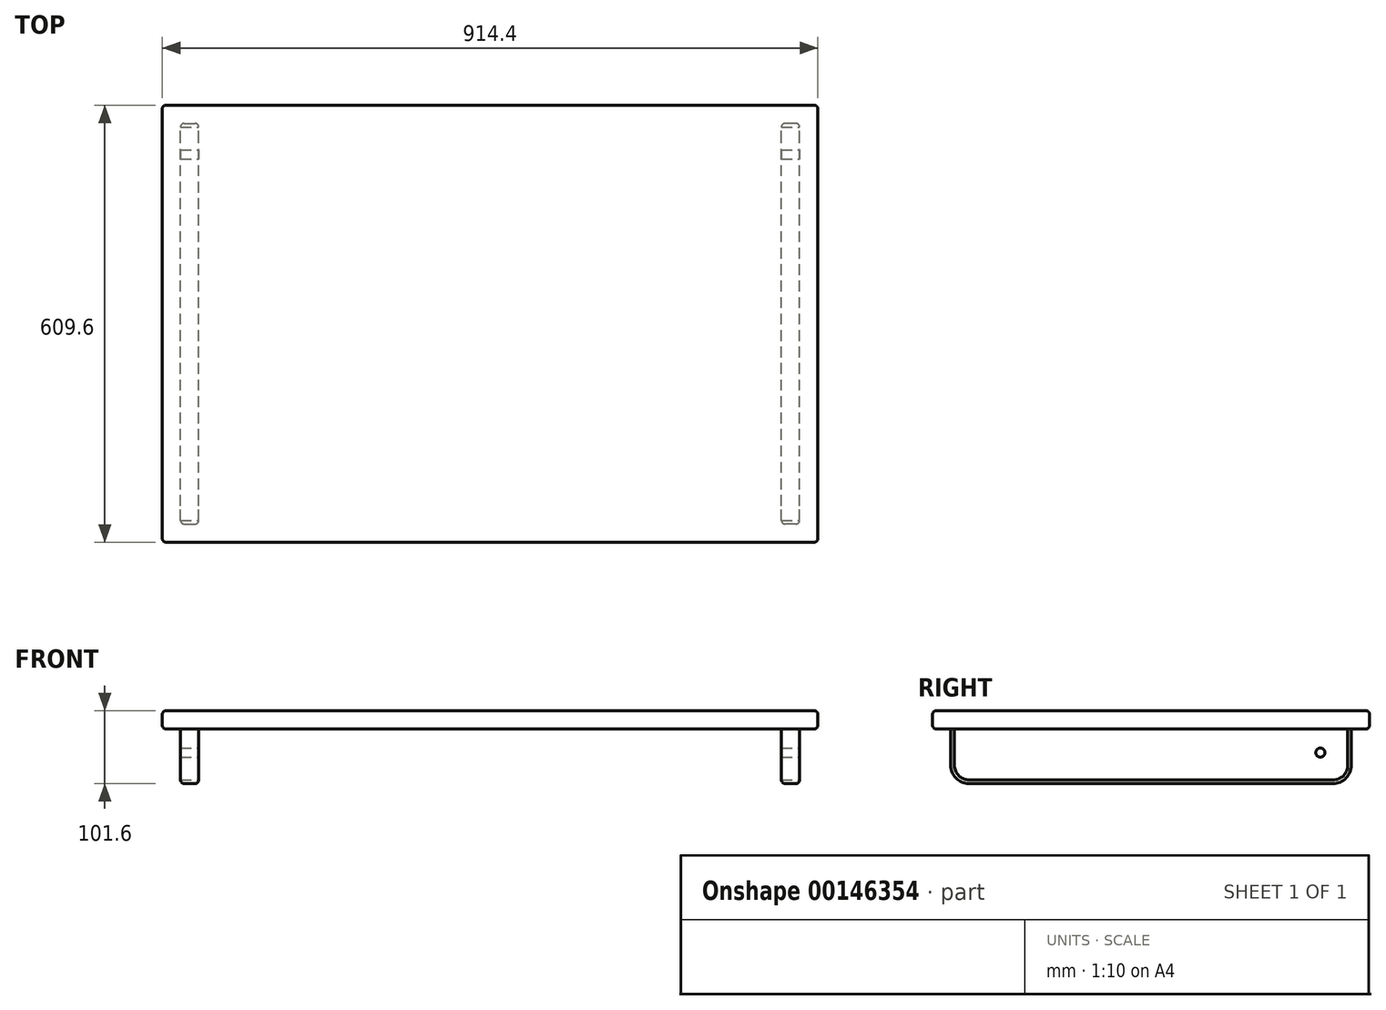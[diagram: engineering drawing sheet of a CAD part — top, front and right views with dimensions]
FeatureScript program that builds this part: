
annotation { "Feature Type Name" : "Feature", "Feature Type Description" : "" }
export const myFeature = defineFeature(function(context is Context, id is Id, definition is map)
    precondition{}
    {
        {
            var Q0;
            Q0=qCreatedBy(makeId("Top.planeOp"),FACE);
            var sketch = newSketch(context, id + "F0", { "sketchPlane" : qUnion([Q0])});
            skLineSegment(sketch, "E0.bottom", {"start": v(-431.8, 279.4) * mm, "end": v(431.8, 279.4) * mm, "construction": true});
            skLineSegment(sketch, "E0.top", {"start": v(-431.8, -279.4) * mm, "end": v(0, -279.4) * mm, "construction": true});
            skLineSegment(sketch, "E0.left", {"start": v(-431.8, 279.4) * mm, "end": v(-431.8, -279.4) * mm, "construction": true});
            skLineSegment(sketch, "E0.right", {"start": v(431.8, 279.4) * mm, "end": v(431.8, 0) * mm, "construction": true});
            skPoint(sketch, "E0.middle", {"position": v(0, 0) * mm});
            skLineSegment(sketch, "E1", {"start": v(0, -279.4) * mm, "end": v(215.9, -279.4) * mm, "construction": true});
            skLineSegment(sketch, "E2", {"start": v(215.9, -279.4) * mm, "end": v(323.85, -279.4) * mm, "construction": true});
            skLineSegment(sketch, "E3", {"start": v(323.85, -279.4) * mm, "end": v(377.82, -279.4) * mm, "construction": true});
            skLineSegment(sketch, "E4", {"start": v(377.82, -279.4) * mm, "end": v(404.81, -279.4) * mm, "construction": true});
            skLineSegment(sketch, "E5", {"start": v(404.81, -279.4) * mm, "end": v(418.3, -279.4) * mm, "construction": true});
            skLineSegment(sketch, "E6", {"start": v(431.8, 0) * mm, "end": v(431.8, -139.7) * mm, "construction": true});
            skLineSegment(sketch, "E7", {"start": v(431.8, -139.7) * mm, "end": v(431.8, -209.55) * mm, "construction": true});
            skLineSegment(sketch, "E8", {"start": v(431.8, -209.55) * mm, "end": v(431.8, -244.48) * mm, "construction": true});
            skLineSegment(sketch, "E9", {"start": v(431.8, -244.48) * mm, "end": v(431.8, -261.94) * mm, "construction": true});
            skLineSegment(sketch, "E10", {"start": v(431.8, -261.94) * mm, "end": v(431.8, -270.67) * mm, "construction": true});
            skLineSegment(sketch, "E11", {"start": v(418.3, -279.4) * mm, "end": v(425.05, -279.4) * mm, "construction": true});
            skLineSegment(sketch, "E12", {"start": v(431.8, -270.67) * mm, "end": v(431.8, -275.03) * mm, "construction": true});
            skLineSegment(sketch, "E13", {"start": v(425.05, -279.4) * mm, "end": v(431.8, -279.4) * mm, "construction": true});
            skLineSegment(sketch, "E14", {"start": v(431.8, -275.03) * mm, "end": v(431.8, -279.4) * mm, "construction": true});
            skLineSegment(sketch, "E15", {"start": v(0, 279.4) * mm, "end": v(0, -279.4) * mm, "construction": true});
            skLineSegment(sketch, "E16", {"start": v(0, 0) * mm, "end": v(431.8, 0) * mm, "construction": true});
            skLineSegment(sketch, "E17", {"start": v(215.9, 0) * mm, "end": v(215.9, -279.4) * mm, "construction": true});
            skLineSegment(sketch, "E18", {"start": v(215.9, -139.7) * mm, "end": v(431.8, -139.7) * mm, "construction": true});
            skLineSegment(sketch, "E19", {"start": v(323.85, -139.7) * mm, "end": v(323.85, -279.4) * mm, "construction": true});
            skLineSegment(sketch, "E20", {"start": v(323.85, -209.55) * mm, "end": v(431.8, -209.55) * mm, "construction": true});
            skLineSegment(sketch, "E21", {"start": v(377.82, -209.55) * mm, "end": v(377.82, -279.4) * mm, "construction": true});
            skLineSegment(sketch, "E22", {"start": v(377.82, -244.48) * mm, "end": v(431.8, -244.48) * mm, "construction": true});
            skLineSegment(sketch, "E23", {"start": v(404.81, -244.48) * mm, "end": v(404.81, -279.4) * mm, "construction": true});
            skLineSegment(sketch, "E24", {"start": v(404.81, -261.94) * mm, "end": v(431.8, -261.94) * mm, "construction": true});
            skLineSegment(sketch, "E25", {"start": v(418.3, -261.94) * mm, "end": v(418.3, -279.4) * mm, "construction": true});
            skLineSegment(sketch, "E26", {"start": v(418.3, -270.67) * mm, "end": v(431.8, -270.67) * mm, "construction": true});
            skLineSegment(sketch, "E27", {"start": v(425.05, -270.67) * mm, "end": v(425.05, -279.4) * mm, "construction": true});
            skLineSegment(sketch, "E28", {"start": v(425.05, -275.03) * mm, "end": v(431.8, -275.03) * mm, "construction": true});
            skSolve(sketch);
        }
        {
            var Q0;
            Q0=qCreatedBy(makeId("Top.planeOp"),FACE);
            var sketch = newSketch(context, id + "F1", { "sketchPlane" : qUnion([Q0])});
            skLineSegment(sketch, "E29.bottom", {"start": v(457.2, 304.8) * mm, "end": v(-457.2, 304.8) * mm});
            skLineSegment(sketch, "E29.top", {"start": v(457.2, -304.8) * mm, "end": v(-457.2, -304.8) * mm});
            skLineSegment(sketch, "E29.left", {"start": v(457.2, 304.8) * mm, "end": v(457.2, -304.8) * mm});
            skLineSegment(sketch, "E29.right", {"start": v(-457.2, 304.8) * mm, "end": v(-457.2, -304.8) * mm});
            skPoint(sketch, "E29.middle", {"position": v(0, 0) * mm});
            skSolve(sketch);
        }
        {
            var Q0;
            Q0=makeQuery(id+"F1.imprint","IMPRINT",FACE,{"disambiguationData":[TD([[makeQuery(id+"F1.imprint","IMPRINT",EDGE,{"derivedFrom":sQuery(id+"F1.wireOp",EDGE,"E29.bottom")}),1.0]])]});
            extrude(context, id + "F2", {"entities" : qUnion([Q0]), "depth" : 25.4 * mm});
        }
        {
            var Q0;
            Q0=makeQuery(id+"F2.opExtrude","SWEPT_EDGE",EDGE,{"disambiguationData":[OSD([sQuery(id+"F1.wireOp",EDGE,"E29.bottom"),sQuery(id+"F1.wireOp",EDGE,"E29.right")])]});
            var Q1;
            Q1=makeQuery(id+"F2.opExtrude","CAP_EDGE",EDGE,{"disambiguationData":[OSD([sQuery(id+"F1.wireOp",EDGE,"E29.right")])],"isStart":false});
            var Q2;
            Q2=makeQuery(id+"F2.opExtrude","SWEPT_EDGE",EDGE,{"disambiguationData":[OSD([sQuery(id+"F1.wireOp",EDGE,"E29.top"),sQuery(id+"F1.wireOp",EDGE,"E29.left")])]});
            var Q3;
            Q3=makeQuery(id+"F2.opExtrude","CAP_EDGE",EDGE,{"disambiguationData":[OSD([sQuery(id+"F1.wireOp",EDGE,"E29.top")])],"isStart":false});
            var Q4;
            Q4=makeQuery(id+"F2.opExtrude","CAP_EDGE",EDGE,{"disambiguationData":[OSD([sQuery(id+"F1.wireOp",EDGE,"E29.right")])],"isStart":true});
            var Q5;
            Q5=makeQuery(id+"F2.opExtrude","CAP_EDGE",EDGE,{"disambiguationData":[OSD([sQuery(id+"F1.wireOp",EDGE,"E29.left")])],"isStart":false});
            var Q6;
            Q6=makeQuery(id+"F2.opExtrude","CAP_EDGE",EDGE,{"disambiguationData":[OSD([sQuery(id+"F1.wireOp",EDGE,"E29.bottom")])],"isStart":false});
            var Q7;
            Q7=makeQuery(id+"F2.opExtrude","SWEPT_EDGE",EDGE,{"disambiguationData":[OSD([sQuery(id+"F1.wireOp",EDGE,"E29.top"),sQuery(id+"F1.wireOp",EDGE,"E29.right")])]});
            var Q8;
            Q8=makeQuery(id+"F2.opExtrude","CAP_EDGE",EDGE,{"disambiguationData":[OSD([sQuery(id+"F1.wireOp",EDGE,"E29.top")])],"isStart":true});
            var Q9;
            Q9=makeQuery(id+"F2.opExtrude","CAP_EDGE",EDGE,{"disambiguationData":[OSD([sQuery(id+"F1.wireOp",EDGE,"E29.bottom")])],"isStart":true});
            var Q10;
            Q10=makeQuery(id+"F2.opExtrude","SWEPT_EDGE",EDGE,{"disambiguationData":[OSD([sQuery(id+"F1.wireOp",EDGE,"E29.bottom"),sQuery(id+"F1.wireOp",EDGE,"E29.left")])]});
            var Q11;
            Q11=makeQuery(id+"F2.opExtrude","CAP_EDGE",EDGE,{"disambiguationData":[OSD([sQuery(id+"F1.wireOp",EDGE,"E29.left")])],"isStart":true});
            fillet(context, id + "F3", {"entities" : qUnion([Q0, Q1, Q2, Q3, Q4, Q5, Q6, Q7, Q8, Q9, Q10, Q11]), "radius" : 5.08 * mm, "tangentPropagation" : true, "allowEdgeOverflow" : false});
        }
        {
            var Q0;
            Q0=qCreatedBy(makeId("Front.planeOp"),FACE);
            var sketch = newSketch(context, id + "F4", { "sketchPlane" : qUnion([Q0])});
            skLineSegment(sketch, "E30.bottom", {"start": v(-431.8, 0) * mm, "end": v(-406.4, 0) * mm});
            skLineSegment(sketch, "E30.top", {"start": v(-431.8, -76.2) * mm, "end": v(-406.4, -76.2) * mm});
            skLineSegment(sketch, "E30.left", {"start": v(-431.8, 0) * mm, "end": v(-431.8, -76.2) * mm});
            skLineSegment(sketch, "E30.right", {"start": v(-406.4, 0) * mm, "end": v(-406.4, -76.2) * mm});
            skLineSegment(sketch, "E31.MirrorCS", {"start": v(431.8, 0) * mm, "end": v(406.4, 0) * mm});
            skLineSegment(sketch, "E32.MirrorCS", {"start": v(431.8, -76.2) * mm, "end": v(406.4, -76.2) * mm});
            skLineSegment(sketch, "E33.MirrorCS", {"start": v(406.4, 0) * mm, "end": v(406.4, -76.2) * mm});
            skLineSegment(sketch, "E34.MirrorCS", {"start": v(431.8, 0) * mm, "end": v(431.8, -76.2) * mm});
            skSolve(sketch);
        }
        {
            var Q0;
            Q0=makeQuery(id+"F4.imprint","IMPRINT",FACE,{"disambiguationData":[TD([[makeQuery(id+"F4.imprint","IMPRINT",EDGE,{"derivedFrom":sQuery(id+"F4.wireOp",EDGE,"E30.bottom")}),-1.0]])]});
            var Q1;
            Q1=makeQuery(id+"F4.imprint","IMPRINT",FACE,{"disambiguationData":[TD([[makeQuery(id+"F4.imprint","IMPRINT",EDGE,{"derivedFrom":sQuery(id+"F4.wireOp",EDGE,"E31.MirrorCS")}),1.0]])]});
            extrude(context, id + "F5", {"entities" : qUnion([Q0, Q1]), "depth" : 558.8 * mm, "symmetric" : true});
        }
        {
            var Q0;
            Q0=makeQuery(id+"F5.opExtrude","CAP_EDGE",EDGE,{"disambiguationData":[OSD([sQuery(id+"F4.wireOp",EDGE,"E30.top")])],"isStart":false});
            var Q1;
            Q1=makeQuery(id+"F5.opExtrude","CAP_EDGE",EDGE,{"disambiguationData":[OSD([sQuery(id+"F4.wireOp",EDGE,"E32.MirrorCS")])],"isStart":false});
            var Q2;
            Q2=makeQuery(id+"F5.opExtrude","CAP_EDGE",EDGE,{"disambiguationData":[OSD([sQuery(id+"F4.wireOp",EDGE,"E32.MirrorCS")])],"isStart":true});
            var Q3;
            Q3=makeQuery(id+"F5.opExtrude","CAP_EDGE",EDGE,{"disambiguationData":[OSD([sQuery(id+"F4.wireOp",EDGE,"E30.top")])],"isStart":true});
            fillet(context, id + "F6", {"entities" : qUnion([Q0, Q1, Q2, Q3]), "radius" : 25.4 * mm, "tangentPropagation" : true, "allowEdgeOverflow" : false});
        }
        {
            var Q0;
            Q0=makeQuery(id+"F6.opFillet","BLEND_EDGE",EDGE,{"blendedFrom":[makeQuery(id+"F5.opExtrude","CAP_EDGE",EDGE,{"disambiguationData":[OSD([sQuery(id+"F4.wireOp",EDGE,"E32.MirrorCS")])],"isStart":false}),makeQuery(id+"F5.opExtrude","SWEPT_FACE",FACE,{"disambiguationData":[OSD([sQuery(id+"F4.wireOp",EDGE,"E34.MirrorCS")])]})],"blendedInto":[makeQuery(id+"F5.opExtrude","SWEPT_FACE",FACE,{"disambiguationData":[OSD([sQuery(id+"F4.wireOp",EDGE,"E34.MirrorCS")])]})]});
            var Q1;
            Q1=makeQuery(id+"F6.opFillet","BLEND_EDGE",EDGE,{"blendedFrom":[makeQuery(id+"F5.opExtrude","CAP_EDGE",EDGE,{"disambiguationData":[OSD([sQuery(id+"F4.wireOp",EDGE,"E32.MirrorCS")])],"isStart":true}),makeQuery(id+"F5.opExtrude","SWEPT_FACE",FACE,{"disambiguationData":[OSD([sQuery(id+"F4.wireOp",EDGE,"E34.MirrorCS")])]})],"blendedInto":[makeQuery(id+"F5.opExtrude","SWEPT_FACE",FACE,{"disambiguationData":[OSD([sQuery(id+"F4.wireOp",EDGE,"E34.MirrorCS")])]})]});
            var Q2;
            Q2=makeQuery(id+"F5.opExtrude","CAP_EDGE",EDGE,{"disambiguationData":[OSD([sQuery(id+"F4.wireOp",EDGE,"E34.MirrorCS")])],"isStart":false});
            var Q3;
            Q3=makeQuery(id+"F5.opExtrude","CAP_EDGE",EDGE,{"disambiguationData":[OSD([sQuery(id+"F4.wireOp",EDGE,"E34.MirrorCS")])],"isStart":true});
            var Q4;
            Q4=makeQuery(id+"F6.opFillet","BLEND_EDGE",EDGE,{"blendedFrom":[makeQuery(id+"F5.opExtrude","CAP_EDGE",EDGE,{"disambiguationData":[OSD([sQuery(id+"F4.wireOp",EDGE,"E32.MirrorCS")])],"isStart":true}),makeQuery(id+"F5.opExtrude","SWEPT_FACE",FACE,{"disambiguationData":[OSD([sQuery(id+"F4.wireOp",EDGE,"E33.MirrorCS")])]})],"blendedInto":[makeQuery(id+"F5.opExtrude","SWEPT_FACE",FACE,{"disambiguationData":[OSD([sQuery(id+"F4.wireOp",EDGE,"E33.MirrorCS")])]})]});
            var Q5;
            Q5=makeQuery(id+"F5.opExtrude","SWEPT_EDGE",EDGE,{"disambiguationData":[OSD([sQuery(id+"F4.wireOp",EDGE,"E32.MirrorCS"),sQuery(id+"F4.wireOp",EDGE,"E34.MirrorCS")])]});
            var Q6;
            Q6=makeQuery(id+"F6.opFillet","BLEND_EDGE",EDGE,{"blendedFrom":[makeQuery(id+"F5.opExtrude","CAP_EDGE",EDGE,{"disambiguationData":[OSD([sQuery(id+"F4.wireOp",EDGE,"E32.MirrorCS")])],"isStart":false}),makeQuery(id+"F5.opExtrude","SWEPT_FACE",FACE,{"disambiguationData":[OSD([sQuery(id+"F4.wireOp",EDGE,"E33.MirrorCS")])]})],"blendedInto":[makeQuery(id+"F5.opExtrude","SWEPT_FACE",FACE,{"disambiguationData":[OSD([sQuery(id+"F4.wireOp",EDGE,"E33.MirrorCS")])]})]});
            var Q7;
            Q7=makeQuery(id+"F6.opFillet","BLEND_EDGE",EDGE,{"blendedFrom":[makeQuery(id+"F5.opExtrude","CAP_EDGE",EDGE,{"disambiguationData":[OSD([sQuery(id+"F4.wireOp",EDGE,"E30.top")])],"isStart":false}),makeQuery(id+"F5.opExtrude","SWEPT_FACE",FACE,{"disambiguationData":[OSD([sQuery(id+"F4.wireOp",EDGE,"E30.right")])]})],"blendedInto":[makeQuery(id+"F5.opExtrude","SWEPT_FACE",FACE,{"disambiguationData":[OSD([sQuery(id+"F4.wireOp",EDGE,"E30.right")])]})]});
            var Q8;
            Q8=makeQuery(id+"F6.opFillet","BLEND_EDGE",EDGE,{"blendedFrom":[makeQuery(id+"F5.opExtrude","CAP_EDGE",EDGE,{"disambiguationData":[OSD([sQuery(id+"F4.wireOp",EDGE,"E30.top")])],"isStart":true}),makeQuery(id+"F5.opExtrude","SWEPT_FACE",FACE,{"disambiguationData":[OSD([sQuery(id+"F4.wireOp",EDGE,"E30.right")])]})],"blendedInto":[makeQuery(id+"F5.opExtrude","SWEPT_FACE",FACE,{"disambiguationData":[OSD([sQuery(id+"F4.wireOp",EDGE,"E30.right")])]})]});
            var Q9;
            Q9=makeQuery(id+"F5.opExtrude","SWEPT_EDGE",EDGE,{"disambiguationData":[OSD([sQuery(id+"F4.wireOp",EDGE,"E32.MirrorCS"),sQuery(id+"F4.wireOp",EDGE,"E33.MirrorCS")])]});
            var Q10;
            Q10=makeQuery(id+"F5.opExtrude","CAP_EDGE",EDGE,{"disambiguationData":[OSD([sQuery(id+"F4.wireOp",EDGE,"E33.MirrorCS")])],"isStart":false});
            var Q11;
            {var subQ0=sQuery(id+"F4.wireOp",EDGE,"E32.MirrorCS");Q11=makeQuery(id+"F6.opFillet","BLEND_EDGE",EDGE,{"blendedFrom":[makeQuery(id+"F5.opExtrude","CAP_EDGE",EDGE,{"disambiguationData":[OSD([subQ0])],"isStart":false}),makeQuery(id+"F5.opExtrude","SWEPT_FACE",FACE,{"disambiguationData":[OSD([subQ0])]})],"blendedInto":[makeQuery(id+"F5.opExtrude","SWEPT_FACE",FACE,{"disambiguationData":[OSD([subQ0])]})]});}
            var Q12;
            {var subQ0=sQuery(id+"F4.wireOp",EDGE,"E32.MirrorCS");Q12=makeQuery(id+"F6.opFillet","BLEND_EDGE",EDGE,{"blendedFrom":[makeQuery(id+"F5.opExtrude","CAP_EDGE",EDGE,{"disambiguationData":[OSD([subQ0])],"isStart":true}),makeQuery(id+"F5.opExtrude","SWEPT_FACE",FACE,{"disambiguationData":[OSD([subQ0])]})],"blendedInto":[makeQuery(id+"F5.opExtrude","SWEPT_FACE",FACE,{"disambiguationData":[OSD([subQ0])]})]});}
            var Q13;
            Q13=makeQuery(id+"F5.opExtrude","CAP_EDGE",EDGE,{"disambiguationData":[OSD([sQuery(id+"F4.wireOp",EDGE,"E33.MirrorCS")])],"isStart":true});
            var Q14;
            {var subQ0=sQuery(id+"F4.wireOp",EDGE,"E32.MirrorCS");Q14=makeQuery(id+"F6.opFillet","BLEND_EDGE",EDGE,{"blendedFrom":[makeQuery(id+"F5.opExtrude","CAP_EDGE",EDGE,{"disambiguationData":[OSD([subQ0])],"isStart":true}),makeQuery(id+"F5.opExtrude","CAP_FACE",FACE,{"disambiguationData":[OSD([sQuery(id+"F4.wireOp",EDGE,"E31.MirrorCS"),subQ0,sQuery(id+"F4.wireOp",EDGE,"E33.MirrorCS"),sQuery(id+"F4.wireOp",EDGE,"E34.MirrorCS")])],"isStart":true})],"blendedInto":[makeQuery(id+"F5.opExtrude","CAP_FACE",FACE,{"disambiguationData":[OSD([sQuery(id+"F4.wireOp",EDGE,"E31.MirrorCS"),subQ0,sQuery(id+"F4.wireOp",EDGE,"E33.MirrorCS"),sQuery(id+"F4.wireOp",EDGE,"E34.MirrorCS")])],"isStart":true})]});}
            var Q15;
            {var subQ0=sQuery(id+"F4.wireOp",EDGE,"E32.MirrorCS");Q15=makeQuery(id+"F6.opFillet","BLEND_EDGE",EDGE,{"blendedFrom":[makeQuery(id+"F5.opExtrude","CAP_EDGE",EDGE,{"disambiguationData":[OSD([subQ0])],"isStart":false}),makeQuery(id+"F5.opExtrude","CAP_FACE",FACE,{"disambiguationData":[OSD([sQuery(id+"F4.wireOp",EDGE,"E31.MirrorCS"),subQ0,sQuery(id+"F4.wireOp",EDGE,"E33.MirrorCS"),sQuery(id+"F4.wireOp",EDGE,"E34.MirrorCS")])],"isStart":false})],"blendedInto":[makeQuery(id+"F5.opExtrude","CAP_FACE",FACE,{"disambiguationData":[OSD([sQuery(id+"F4.wireOp",EDGE,"E31.MirrorCS"),subQ0,sQuery(id+"F4.wireOp",EDGE,"E33.MirrorCS"),sQuery(id+"F4.wireOp",EDGE,"E34.MirrorCS")])],"isStart":false})]});}
            var Q16;
            Q16=makeQuery(id+"F6.opFillet","BLEND_EDGE",EDGE,{"blendedFrom":[makeQuery(id+"F5.opExtrude","CAP_EDGE",EDGE,{"disambiguationData":[OSD([sQuery(id+"F4.wireOp",EDGE,"E30.top")])],"isStart":true}),makeQuery(id+"F5.opExtrude","SWEPT_FACE",FACE,{"disambiguationData":[OSD([sQuery(id+"F4.wireOp",EDGE,"E30.left")])]})],"blendedInto":[makeQuery(id+"F5.opExtrude","SWEPT_FACE",FACE,{"disambiguationData":[OSD([sQuery(id+"F4.wireOp",EDGE,"E30.left")])]})]});
            var Q17;
            Q17=makeQuery(id+"F6.opFillet","BLEND_EDGE",EDGE,{"blendedFrom":[makeQuery(id+"F5.opExtrude","CAP_EDGE",EDGE,{"disambiguationData":[OSD([sQuery(id+"F4.wireOp",EDGE,"E30.top")])],"isStart":false}),makeQuery(id+"F5.opExtrude","SWEPT_FACE",FACE,{"disambiguationData":[OSD([sQuery(id+"F4.wireOp",EDGE,"E30.left")])]})],"blendedInto":[makeQuery(id+"F5.opExtrude","SWEPT_FACE",FACE,{"disambiguationData":[OSD([sQuery(id+"F4.wireOp",EDGE,"E30.left")])]})]});
            var Q18;
            Q18=makeQuery(id+"F5.opExtrude","CAP_EDGE",EDGE,{"disambiguationData":[OSD([sQuery(id+"F4.wireOp",EDGE,"E30.right")])],"isStart":true});
            var Q19;
            Q19=makeQuery(id+"F5.opExtrude","SWEPT_EDGE",EDGE,{"disambiguationData":[OSD([sQuery(id+"F4.wireOp",EDGE,"E30.top"),sQuery(id+"F4.wireOp",EDGE,"E30.right")])]});
            var Q20;
            Q20=makeQuery(id+"F5.opExtrude","CAP_EDGE",EDGE,{"disambiguationData":[OSD([sQuery(id+"F4.wireOp",EDGE,"E30.right")])],"isStart":false});
            var Q21;
            {var subQ0=sQuery(id+"F4.wireOp",EDGE,"E30.top");Q21=makeQuery(id+"F6.opFillet","BLEND_EDGE",EDGE,{"blendedFrom":[makeQuery(id+"F5.opExtrude","CAP_EDGE",EDGE,{"disambiguationData":[OSD([subQ0])],"isStart":false}),makeQuery(id+"F5.opExtrude","CAP_FACE",FACE,{"disambiguationData":[OSD([sQuery(id+"F4.wireOp",EDGE,"E30.bottom"),subQ0,sQuery(id+"F4.wireOp",EDGE,"E30.left"),sQuery(id+"F4.wireOp",EDGE,"E30.right")])],"isStart":false})],"blendedInto":[makeQuery(id+"F5.opExtrude","CAP_FACE",FACE,{"disambiguationData":[OSD([sQuery(id+"F4.wireOp",EDGE,"E30.bottom"),subQ0,sQuery(id+"F4.wireOp",EDGE,"E30.left"),sQuery(id+"F4.wireOp",EDGE,"E30.right")])],"isStart":false})]});}
            var Q22;
            {var subQ0=sQuery(id+"F4.wireOp",EDGE,"E30.top");Q22=makeQuery(id+"F6.opFillet","BLEND_EDGE",EDGE,{"blendedFrom":[makeQuery(id+"F5.opExtrude","CAP_EDGE",EDGE,{"disambiguationData":[OSD([subQ0])],"isStart":true}),makeQuery(id+"F5.opExtrude","CAP_FACE",FACE,{"disambiguationData":[OSD([sQuery(id+"F4.wireOp",EDGE,"E30.bottom"),subQ0,sQuery(id+"F4.wireOp",EDGE,"E30.left"),sQuery(id+"F4.wireOp",EDGE,"E30.right")])],"isStart":true})],"blendedInto":[makeQuery(id+"F5.opExtrude","CAP_FACE",FACE,{"disambiguationData":[OSD([sQuery(id+"F4.wireOp",EDGE,"E30.bottom"),subQ0,sQuery(id+"F4.wireOp",EDGE,"E30.left"),sQuery(id+"F4.wireOp",EDGE,"E30.right")])],"isStart":true})]});}
            var Q23;
            Q23=makeQuery(id+"F5.opExtrude","CAP_EDGE",EDGE,{"disambiguationData":[OSD([sQuery(id+"F4.wireOp",EDGE,"E30.left")])],"isStart":true});
            var Q24;
            {var subQ0=sQuery(id+"F4.wireOp",EDGE,"E30.top");Q24=makeQuery(id+"F6.opFillet","BLEND_EDGE",EDGE,{"blendedFrom":[makeQuery(id+"F5.opExtrude","CAP_EDGE",EDGE,{"disambiguationData":[OSD([subQ0])],"isStart":false}),makeQuery(id+"F5.opExtrude","SWEPT_FACE",FACE,{"disambiguationData":[OSD([subQ0])]})],"blendedInto":[makeQuery(id+"F5.opExtrude","SWEPT_FACE",FACE,{"disambiguationData":[OSD([subQ0])]})]});}
            var Q25;
            Q25=makeQuery(id+"F5.opExtrude","CAP_EDGE",EDGE,{"disambiguationData":[OSD([sQuery(id+"F4.wireOp",EDGE,"E30.left")])],"isStart":false});
            var Q26;
            {var subQ0=sQuery(id+"F4.wireOp",EDGE,"E30.top");Q26=makeQuery(id+"F6.opFillet","BLEND_EDGE",EDGE,{"blendedFrom":[makeQuery(id+"F5.opExtrude","CAP_EDGE",EDGE,{"disambiguationData":[OSD([subQ0])],"isStart":true}),makeQuery(id+"F5.opExtrude","SWEPT_FACE",FACE,{"disambiguationData":[OSD([subQ0])]})],"blendedInto":[makeQuery(id+"F5.opExtrude","SWEPT_FACE",FACE,{"disambiguationData":[OSD([subQ0])]})]});}
            var Q27;
            Q27=makeQuery(id+"F5.opExtrude","SWEPT_EDGE",EDGE,{"disambiguationData":[OSD([sQuery(id+"F4.wireOp",EDGE,"E30.top"),sQuery(id+"F4.wireOp",EDGE,"E30.left")])]});
            fillet(context, id + "F7", {"entities" : qUnion([Q0, Q1, Q2, Q3, Q4, Q5, Q6, Q7, Q8, Q9, Q10, Q11, Q12, Q13, Q14, Q15, Q16, Q17, Q18, Q19, Q20, Q21, Q22, Q23, Q24, Q25, Q26, Q27]), "radius" : 5.08 * mm, "tangentPropagation" : true, "allowEdgeOverflow" : false});
        }
        {
            var Q0;
            Q0=makeQuery(id+"F5.opExtrude","SWEPT_FACE",FACE,{"disambiguationData":[OSD([sQuery(id+"F4.wireOp",EDGE,"E34.MirrorCS")])]});
            var sketch = newSketch(context, id + "F8", { "sketchPlane" : qUnion([Q0])});
            skCircle(sketch, "E35", {"center": v(-236.22, -33.02) * mm, "radius": 6.35 * mm});
            skCircle(sketch, "E36.MirrorC", {"center": v(236.22, -33.02) * mm, "radius": 6.35 * mm});
            skSolve(sketch);
        }
        {
            var Q0;
            Q0=makeQuery(id+"F8.imprint","IMPRINT",FACE,{"disambiguationData":[TD([[makeQuery(id+"F8.imprint","IMPRINT",EDGE,{"derivedFrom":sQuery(id+"F8.wireOp",EDGE,"E35")}),1.0]])]});
            var Q1;
            Q1=makeQuery(id+"F8.imprint","IMPRINT",FACE,{"disambiguationData":[TD([[makeQuery(id+"F8.imprint","IMPRINT",EDGE,{"derivedFrom":sQuery(id+"F8.wireOp",EDGE,"E36.MirrorC")}),-1.0]])]});
            var Q2;
            Q2=makeQuery(id+"F5.opExtrude","SWEPT_FACE",FACE,{"disambiguationData":[OSD([sQuery(id+"F4.wireOp",EDGE,"E30.left")])]});
            extrude(context, id + "F9", {"entities" : qUnion([Q0, Q1]), "operationType" : NewBodyOperationType.REMOVE, "endBound" : BoundingType.UP_TO_SURFACE, "oppositeDirection" : true, "endBoundEntityFace" : qUnion([Q2]), "depth" : 25.4 * mm});
        }
    });
